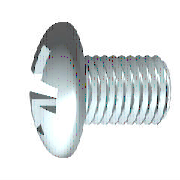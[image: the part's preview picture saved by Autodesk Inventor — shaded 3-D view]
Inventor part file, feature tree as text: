
AUTODESK INVENTOR PART (.ipt)
format: ipt  version: 2024 (Build 280153000, 153)  size: 259,072 bytes
history: native  units: mm (DEFAULTED — no unit token found)
features: extrude x1, other x1, plane x1
ambient origin geometry x7: Origin, YZ Plane, XZ Plane, X Axis, Y Axis, Z Axis, Center Point
bodies: Solid1 (feature_tree), Body (feature_tree)
feature tree (3):
  extrude  "Slot"  Depth=4.0mm
  other  "Cut"
  plane  "Work Plane3"
